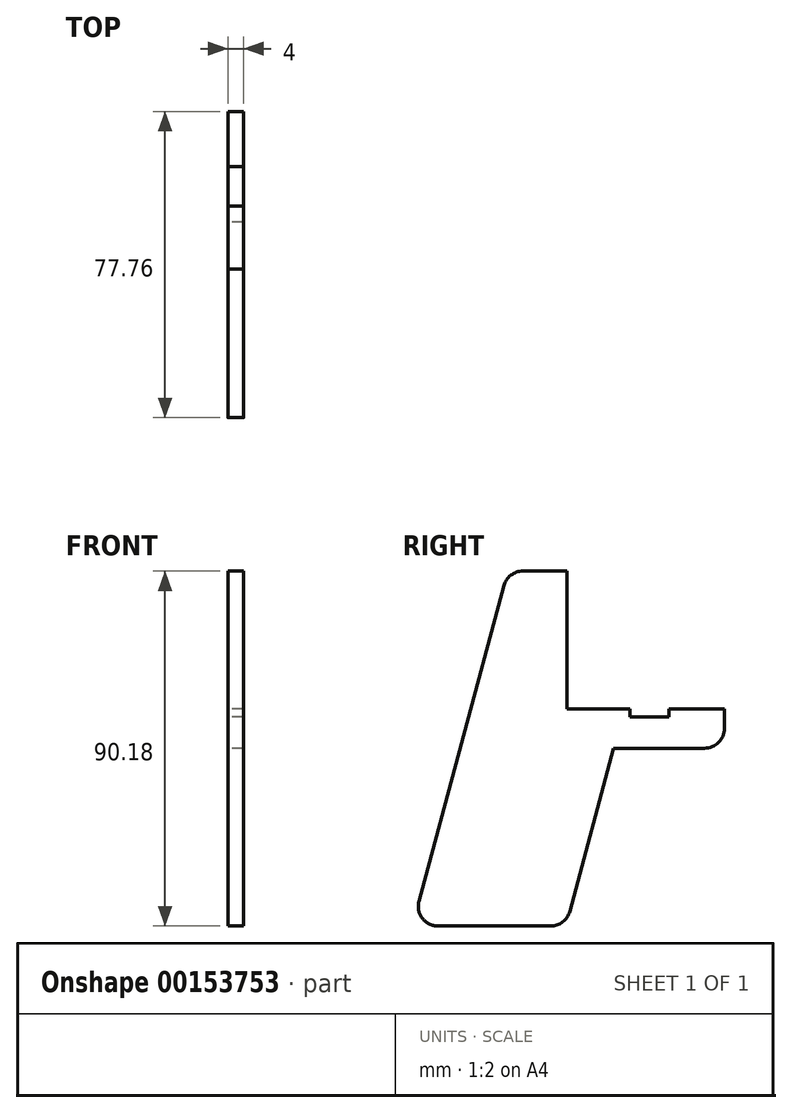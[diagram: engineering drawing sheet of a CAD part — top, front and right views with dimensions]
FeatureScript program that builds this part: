
annotation { "Feature Type Name" : "Feature", "Feature Type Description" : "" }
export const myFeature = defineFeature(function(context is Context, id is Id, definition is map)
    precondition{}
    {
        {
            var Q0;
            Q0=qCreatedBy(makeId("Right.planeOp"),FACE);
            var sketch = newSketch(context, id + "F0", { "sketchPlane" : qUnion([Q0])});
            skLineSegment(sketch, "E0", {"start": v(0, 0) * mm, "end": v(0, 35) * mm});
            skLineSegment(sketch, "E1", {"start": v(0, 35) * mm, "end": v(-11.17, 35) * mm});
            skLineSegment(sketch, "E2", {"start": v(40, 0) * mm, "end": v(40, -5) * mm});
            skLineSegment(sketch, "E3", {"start": v(35, -10) * mm, "end": v(11.9, -10) * mm});
            skLineSegment(sketch, "E4", {"start": v(11.9, -10) * mm, "end": v(0.72, -51.48) * mm});
            skPoint(sketch, "E5.orphan", {"position": v(0, -10) * mm});
            skLineSegment(sketch, "E6", {"start": v(-16, 31.3) * mm, "end": v(-37.59, -48.88) * mm});
            skLineSegment(sketch, "E7", {"start": v(-32.76, -55.18) * mm, "end": v(-4.1, -55.18) * mm});
            skPoint(sketch, "E8.visualSharp", {"position": v(40, -10) * mm});
            skArc(sketch, "E8.filletArc", {"start": v(35, -10) * mm, "mid": v(38.54, -8.54) * mm, "end": v(40, -5) * mm});
            skArc(sketch, "E9.filletArc", {"start": v(-4.1, -55.18) * mm, "mid": v(-1.06, -54.14) * mm, "end": v(0.72, -51.48) * mm});
            skArc(sketch, "E10.filletArc", {"start": v(-37.59, -48.88) * mm, "mid": v(-36.73, -53.22) * mm, "end": v(-32.76, -55.18) * mm});
            skPoint(sketch, "E11.visualSharp", {"position": v(-15, 35) * mm});
            skArc(sketch, "E11.filletArc", {"start": v(-11.17, 35) * mm, "mid": v(-14.2, 33.97) * mm, "end": v(-16, 31.3) * mm});
            skLineSegment(sketch, "E12", {"start": v(0, 0) * mm, "end": v(0, -2) * mm});
            skLineSegment(sketch, "E13.trimOffspring", {"start": v(0, 0) * mm, "end": v(16, 0) * mm});
            skLineSegment(sketch, "E14", {"start": v(26, 0) * mm, "end": v(26, -2) * mm});
            skLineSegment(sketch, "E15", {"start": v(26, -2) * mm, "end": v(16, -2) * mm});
            skLineSegment(sketch, "E16", {"start": v(16, -2) * mm, "end": v(16, 0) * mm});
            skPoint(sketch, "E16.endSnap0", {"position": v(20, 0) * mm});
            skLineSegment(sketch, "E17.trimOffspring", {"start": v(26, 0) * mm, "end": v(40, 0) * mm});
            skSolve(sketch);
        }
        {
            var Q0;
            Q0=makeQuery(id+"F0.imprint","IMPRINT",FACE,{"disambiguationData":[TD([[makeQuery(id+"F0.imprint","IMPRINT",EDGE,{"derivedFrom":sQuery(id+"F0.wireOp",EDGE,"E0")}),1.0]])]});
            extrude(context, id + "F1", {"entities" : qUnion([Q0]), "depth" : 4 * mm});
        }
    });
